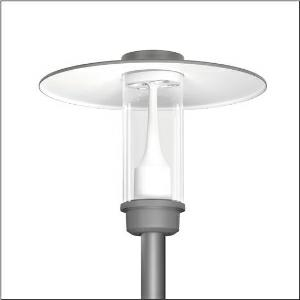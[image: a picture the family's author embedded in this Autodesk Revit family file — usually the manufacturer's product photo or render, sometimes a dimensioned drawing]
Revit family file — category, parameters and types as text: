
# Revit family: litepole_2_iq___st1_2a_5xa5425af14hp_29a9
name_source: partatom
category: Lighting Fixtures
units: mm (PartAtom-declared; Revit-internal decimal feet)

## family parameters
Cut with Voids When Loaded = No
Host = Face
Light Source = No
Part Type = Normal
Room Calculation Point = No
Round Connector Dimension = Use Diameter
Shared = No

## types (1)
- --- (1 x LED, 3940 lm, 33.6 W, 2200K)
    Apparent Load = 34 VA
    CIE Flux Codes = 22 59 92 98 100
    Color Rendering = 70
    Color Temperature = 2200K
    Default Elevation = 1800 mm
    Description = Litepole 2 iQ, mast luminaire, Module 540 iQ-SR, primary light control with 3 zone facetted reflector, of plastic, silver coated, highly specular, structured, primary optical cover: cover, of PMMA, transparent, light distribution: ST1.2a, light emission: direct distribution, primary light characteristic: asymmetric, installation type: post-top, LED, High Power LED, rated luminous flux: 3.940lm, luminous efficacy: 117lm/W, light colour: 722, colour temperature: 2200K, control gear: iQ Street-Remote, control: pre-setting: logarithmic dimming characteristic, Street-Remote, Auto-Match, Temp-Guard, Lumen-Switch, Night-Set, Smart-Wire, Light-Fading, Desk-Remote (wireless, voltage-free reading and setting of iQ features in the workshop via application-optimized NFC function/RFID function), optimised constant luminous flux control (CLO 2.0), with terminal, 6-pole, max. 2.5mm², mains connection: 230..240V, AC, 50/60Hz, start of lifetime: 34W, end of service life: 36W, reduction: 15W, luminaire housing, upper part, of aluminium, coated, Siteco® metallic grey (DB 702S), diameter: 750mm, height: 590mm, spigot size: d x l = 76 x 70mm (post-top) | with reducer (optional accessory) 60 x 70mm, mounting height: 3..5m, post-top mast mounting element, of diecast aluminium, coated, Siteco® metallic grey (DB 702S), Module 540 iQ-SR, traffic white (RAL 9016), equipment: Power, protection rating (complete): IP65, insulation class (complete): insulation class II (safety insulation), certification: CE, ENEC, VDE, packaging unit: 1 piece

Light Distribution: ST1.2a
    Height = 590 mm
    Lamp = 1 x LED
    Lamp Light Flux = 3940 lm
    Lamp Power = 33.6 W
    Lamp count = 1
    Length = 750 mm
    Luminous efficacy = 117 lm/W
    Manufacturer = Siteco
    ModVariant = No
    Model = 5XA5425AF14HP
    Number of Poles = 1
    OnlyDefault = Yes
    Power Factor = 1
    Product Name = Litepole 2 iQ | ST1.2a
    Product group = mast luminaire | pylon top
    ProductGroupID = 6100
    Protection Class = Protection class II
    Protection Degree = IP 65
    RLX_Detail_Level = 1
    RLX_Emergency_Light_Flux = 0 lm
    RLX_Emergency_Type = 0
    RLX_Emergency_Type_DB = No
    RlxData = <blob elided: 31961 chars, md5=69986ecf>
    Socket = socket
    Standby Power = 0 W
    System Light Flux = 3940 lm
    System Power = 34 W
    Type Comments = factory setting: luminous flux: 100 % | dim-lin: 254 | 695 mA
    Type Image = l_1006518.jpg
    URL = http://relux.com
    VarID = @adj_213597
    Voltage = 0 V
    Weight = 0.00 kg
    Width = 0 mm  [stored 0 ft]

note: [stored X ft] marks values corroborated as IEEE doubles in the binary element streams (Revit-internal decimal feet)

## geometry (parser evidence)
native form markers: Blend x4, Sweep x10
no freeform markers — native parametric forms only
